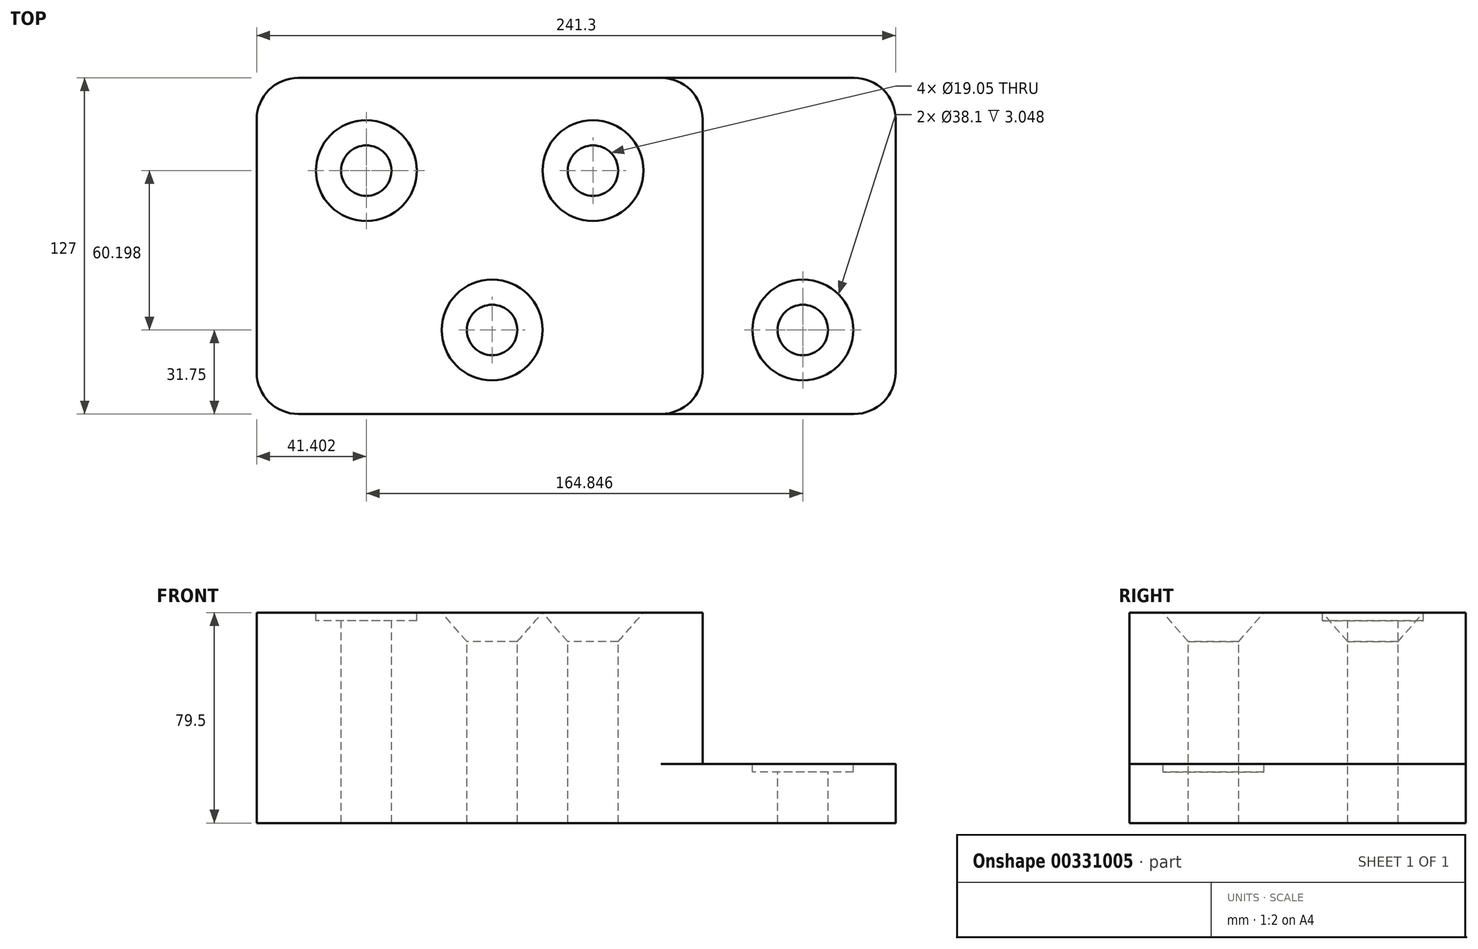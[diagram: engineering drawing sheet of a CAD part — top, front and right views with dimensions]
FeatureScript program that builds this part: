
annotation { "Feature Type Name" : "Feature", "Feature Type Description" : "" }
export const myFeature = defineFeature(function(context is Context, id is Id, definition is map)
    precondition{}
    {
        {
            var Q0;
            Q0=qCreatedBy(makeId("Top.planeOp"),FACE);
            var sketch = newSketch(context, id + "F0", { "sketchPlane" : qUnion([Q0])});
            skLineSegment(sketch, "E0.bottom", {"start": v(15.75, 0) * mm, "end": v(152.65, 0) * mm});
            skLineSegment(sketch, "E0.top", {"start": v(15.75, 127) * mm, "end": v(152.65, 127) * mm});
            skLineSegment(sketch, "E0.left", {"start": v(0, 15.75) * mm, "end": v(0, 111.25) * mm});
            skLineSegment(sketch, "E0.right", {"start": v(168.4, 15.75) * mm, "end": v(168.4, 111.25) * mm});
            skPoint(sketch, "E1.visualSharp", {"position": v(0, 127) * mm});
            skArc(sketch, "E1.filletArc", {"start": v(15.75, 127) * mm, "mid": v(4.61, 122.39) * mm, "end": v(0, 111.25) * mm});
            skPoint(sketch, "E2.visualSharp", {"position": v(168.4, 127) * mm});
            skArc(sketch, "E2.filletArc", {"start": v(168.4, 111.25) * mm, "mid": v(163.79, 122.39) * mm, "end": v(152.65, 127) * mm});
            skPoint(sketch, "E3.visualSharp", {"position": v(0, 0) * mm});
            skArc(sketch, "E3.filletArc", {"start": v(0, 15.75) * mm, "mid": v(4.61, 4.61) * mm, "end": v(15.75, 0) * mm});
            skPoint(sketch, "E4.visualSharp", {"position": v(168.4, 0) * mm});
            skArc(sketch, "E4.filletArc", {"start": v(152.65, 0) * mm, "mid": v(163.79, 4.61) * mm, "end": v(168.4, 15.75) * mm});
            skLineSegment(sketch, "E5", {"start": v(152.65, 127) * mm, "end": v(225.55, 127) * mm});
            skLineSegment(sketch, "E6", {"start": v(241.3, 111.25) * mm, "end": v(241.3, 15.75) * mm});
            skLineSegment(sketch, "E7", {"start": v(225.55, 0) * mm, "end": v(152.65, 0) * mm});
            skPoint(sketch, "E8.visualSharp", {"position": v(241.3, 127) * mm});
            skArc(sketch, "E8.filletArc", {"start": v(241.3, 111.25) * mm, "mid": v(236.69, 122.39) * mm, "end": v(225.55, 127) * mm});
            skPoint(sketch, "E9.visualSharp", {"position": v(241.3, 0) * mm});
            skArc(sketch, "E9.filletArc", {"start": v(225.55, 0) * mm, "mid": v(236.69, 4.61) * mm, "end": v(241.3, 15.75) * mm});
            skSolve(sketch);
        }
        {
            var Q0;
            Q0=makeQuery(id+"F0.imprint","IMPRINT",FACE,{"disambiguationData":[TD([[makeQuery(id+"F0.imprint","IMPRINT",EDGE,{"derivedFrom":sQuery(id+"F0.wireOp",EDGE,"E0.bottom")}),1.0]])]});
            extrude(context, id + "F1", {"entities" : qUnion([Q0]), "depth" : 79.5 * mm});
        }
        {
            var Q0;
            Q0 = qSketchRegion(id + "F0", true);
            extrude(context, id + "F2", {"entities" : qUnion([Q0]), "operationType" : NewBodyOperationType.ADD, "depth" : 22.35 * mm});
        }
        {
            var Q0;
            Q0=makeQuery(id+"F2.opExtrude","CAP_FACE",FACE,{"disambiguationData":[OSD([sQuery(id+"F0.wireOp",EDGE,"E0.bottom"),sQuery(id+"F0.wireOp",EDGE,"E0.top"),sQuery(id+"F0.wireOp",EDGE,"E0.left"),sQuery(id+"F0.wireOp",EDGE,"E1.filletArc"),sQuery(id+"F0.wireOp",EDGE,"E3.filletArc"),sQuery(id+"F0.wireOp",EDGE,"E5"),sQuery(id+"F0.wireOp",EDGE,"E6"),sQuery(id+"F0.wireOp",EDGE,"E7"),sQuery(id+"F0.wireOp",EDGE,"E8.filletArc"),sQuery(id+"F0.wireOp",EDGE,"E9.filletArc")])],"isStart":false});
            var sketch = newSketch(context, id + "F3", { "sketchPlane" : qUnion([Q0])});
            skCircle(sketch, "E10", {"center": v(206.25, 31.75) * mm, "radius": 19.05 * mm});
            skCircle(sketch, "E11", {"center": v(206.25, 31.75) * mm, "radius": 9.53 * mm});
            skSolve(sketch);
        }
        {
            var Q0;
            Q0=makeQuery(id+"F1.opExtrude","CAP_FACE",FACE,{"disambiguationData":[OSD([sQuery(id+"F0.wireOp",EDGE,"E0.bottom"),sQuery(id+"F0.wireOp",EDGE,"E0.top"),sQuery(id+"F0.wireOp",EDGE,"E0.left"),sQuery(id+"F0.wireOp",EDGE,"E0.right"),sQuery(id+"F0.wireOp",EDGE,"E1.filletArc"),sQuery(id+"F0.wireOp",EDGE,"E2.filletArc"),sQuery(id+"F0.wireOp",EDGE,"E3.filletArc"),sQuery(id+"F0.wireOp",EDGE,"E4.filletArc")])],"isStart":false});
            var sketch = newSketch(context, id + "F4", { "sketchPlane" : qUnion([Q0])});
            skCircle(sketch, "E12", {"center": v(41.4, 91.95) * mm, "radius": 19.05 * mm});
            skCircle(sketch, "E13", {"center": v(41.4, 91.95) * mm, "radius": 9.53 * mm});
            skPoint(sketch, "E14", {"position": v(127, 91.95) * mm});
            skPoint(sketch, "E15", {"position": v(88.9, 31.75) * mm});
            skSolve(sketch);
        }
        {
            var Q0;
            Q0=makeQuery(id+"F4.imprint","IMPRINT",FACE,{"disambiguationData":[TD([[makeQuery(id+"F4.imprint","IMPRINT",EDGE,{"derivedFrom":sQuery(id+"F4.wireOp",EDGE,"E13")}),1.0]])]});
            var Q1;
            Q1=makeQuery(id+"F3.imprint","IMPRINT",FACE,{"disambiguationData":[TD([[makeQuery(id+"F3.imprint","IMPRINT",EDGE,{"derivedFrom":sQuery(id+"F3.wireOp",EDGE,"E11")}),1.0]])]});
            extrude(context, id + "F5", {"entities" : qUnion([Q0, Q1]), "operationType" : NewBodyOperationType.REMOVE, "endBound" : BoundingType.THROUGH_ALL, "oppositeDirection" : true, "depth" : 25.4 * mm});
        }
        {
            var Q0;
            Q0=makeQuery(id+"F4.imprint","IMPRINT",FACE,{"disambiguationData":[TD([[makeQuery(id+"F4.imprint","IMPRINT",EDGE,{"derivedFrom":sQuery(id+"F4.wireOp",EDGE,"E12")}),1.0]])]});
            var Q1;
            Q1=makeQuery(id+"F3.imprint","IMPRINT",FACE,{"disambiguationData":[TD([[makeQuery(id+"F3.imprint","IMPRINT",EDGE,{"derivedFrom":sQuery(id+"F3.wireOp",EDGE,"E10")}),1.0]])]});
            extrude(context, id + "F6", {"entities" : qUnion([Q0, Q1]), "operationType" : NewBodyOperationType.REMOVE, "oppositeDirection" : true, "depth" : 3.05 * mm});
        }
        {
            var Q0;
            Q0=sQuery(id+"F4.wireOp",VERTEX,"E15");
            var Q1;
            Q1=sQuery(id+"F4.wireOp",VERTEX,"E14");
            var Q2;
            Q2=makeQuery(id+"F1.opExtrude","SWEPT_BODY",BODY,{"disambiguationData":[OSD([sQuery(id+"F0.wireOp",EDGE,"E0.bottom"),sQuery(id+"F0.wireOp",EDGE,"E0.top"),sQuery(id+"F0.wireOp",EDGE,"E0.left"),sQuery(id+"F0.wireOp",EDGE,"E0.right"),sQuery(id+"F0.wireOp",EDGE,"E1.filletArc"),sQuery(id+"F0.wireOp",EDGE,"E2.filletArc"),sQuery(id+"F0.wireOp",EDGE,"E3.filletArc"),sQuery(id+"F0.wireOp",EDGE,"E4.filletArc")])]});
            hole(context, id + "F7", {"style" : HoleStyle.C_SINK, "endStyle" : HoleEndStyle.THROUGH, "holeDiameter" : 19.05 * mm, "cSinkDiameter" : 38.1 * mm, "cSinkAngle" : 82 * degree, "tappedDepth" : 12.7 * mm, "tapClearance" : 3, "locations" : qUnion([Q0, Q1]), "scope" : qUnion([Q2])});
        }
    });
